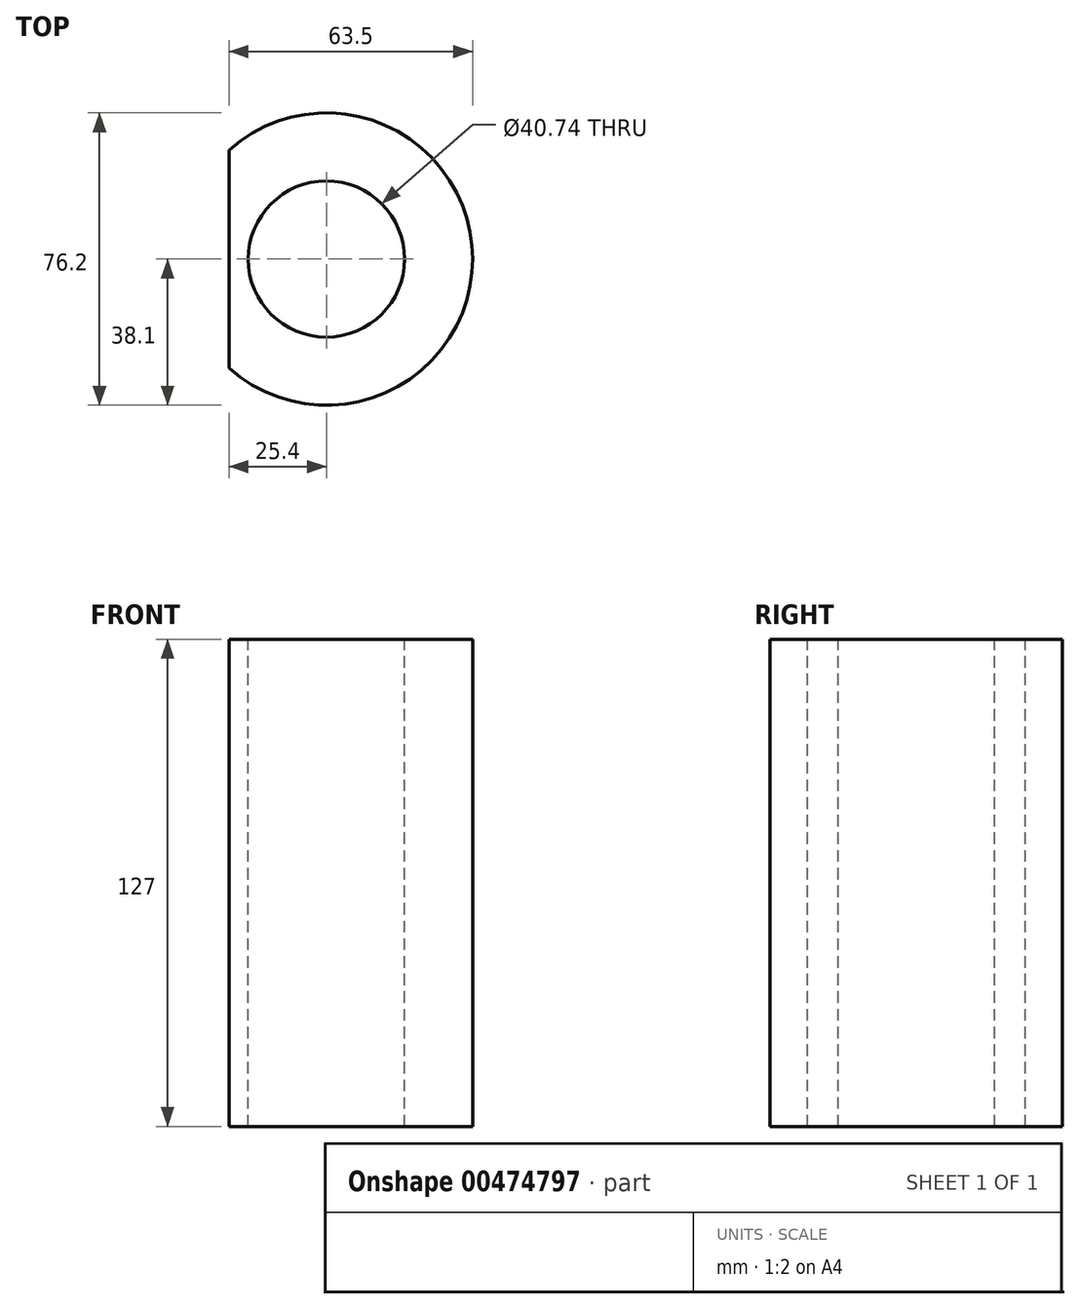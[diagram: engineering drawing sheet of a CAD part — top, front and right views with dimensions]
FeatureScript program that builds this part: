
annotation { "Feature Type Name" : "Feature", "Feature Type Description" : "" }
export const myFeature = defineFeature(function(context is Context, id is Id, definition is map)
    precondition{}
    {
        {
            var Q0;
            Q0=qCreatedBy(makeId("Top.planeOp"),FACE);
            var sketch = newSketch(context, id + "F0", { "sketchPlane" : qUnion([Q0])});
            skCircle(sketch, "E0", {"center": v(0, 0) * mm, "radius": 38.1 * mm});
            skSolve(sketch);
        }
        {
            var Q0;
            Q0=makeQuery(id+"F0.imprint","IMPRINT",FACE,{"disambiguationData":[TD([[makeQuery(id+"F0.imprint","IMPRINT",EDGE,{"derivedFrom":sQuery(id+"F0.wireOp",EDGE,"E0")}),1.0]])]});
            extrude(context, id + "F1", {"entities" : qUnion([Q0]), "depth" : 127 * mm, "hasSecondDirection" : true, "secondDirectionOppositeDirection" : false, "secondDirectionDepth" : 0 * mm});
        }
        {
            var Q0;
            Q0=makeQuery(id+"F1.opExtrude","CAP_FACE",FACE,{"disambiguationData":[OSD([sQuery(id+"F0.wireOp",EDGE,"E0")])],"isStart":false});
            var sketch = newSketch(context, id + "F2", { "sketchPlane" : qUnion([Q0])});
            skCircle(sketch, "E1", {"center": v(0, 0) * mm, "radius": 20.37 * mm});
            skSolve(sketch);
        }
        {
            var Q0;
            Q0=makeQuery(id+"F2.imprint","IMPRINT",FACE,{"disambiguationData":[TD([[makeQuery(id+"F2.imprint","IMPRINT",EDGE,{"derivedFrom":sQuery(id+"F2.wireOp",EDGE,"E1")}),1.0]])]});
            var Q1;
            Q1=sQuery(id+"F2.wireOp",EDGE,"E1");
            extrude(context, id + "F3", {"entities" : qUnion([Q0]), "operationType" : NewBodyOperationType.REMOVE, "surfaceEntities" : qUnion([Q1]), "endBound" : BoundingType.THROUGH_ALL, "oppositeDirection" : true, "depth" : 25.4 * mm});
        }
        {
            var Q0;
            Q0=makeQuery(id+"F2.imprint","IMPRINT",FACE,{"disambiguationData":[TD([[makeQuery(id+"F2.imprint","IMPRINT",EDGE,{"derivedFrom":sQuery(id+"F2.wireOp",EDGE,"E1")}),-1.0]])]});
            var sketch = newSketch(context, id + "F4", { "sketchPlane" : qUnion([Q0])});
            skLineSegment(sketch, "E2", {"start": v(-25.4, -28.4) * mm, "end": v(-25.4, 28.4) * mm});
            skArc(sketch, "E3", {"start": v(-25.4, 28.4) * mm, "mid": v(-38.1, 0) * mm, "end": v(-25.4, -28.4) * mm});
            skSolve(sketch);
        }
        {
            var Q0;
            Q0=makeQuery(id+"F4.imprint","IMPRINT",FACE,{"disambiguationData":[TD([[makeQuery(id+"F4.imprint","IMPRINT",EDGE,{"derivedFrom":sQuery(id+"F4.wireOp",EDGE,"E2")}),1.0]])]});
            extrude(context, id + "F5", {"entities" : qUnion([Q0]), "operationType" : NewBodyOperationType.REMOVE, "endBound" : BoundingType.THROUGH_ALL, "oppositeDirection" : true, "depth" : 25.4 * mm});
        }
    });
